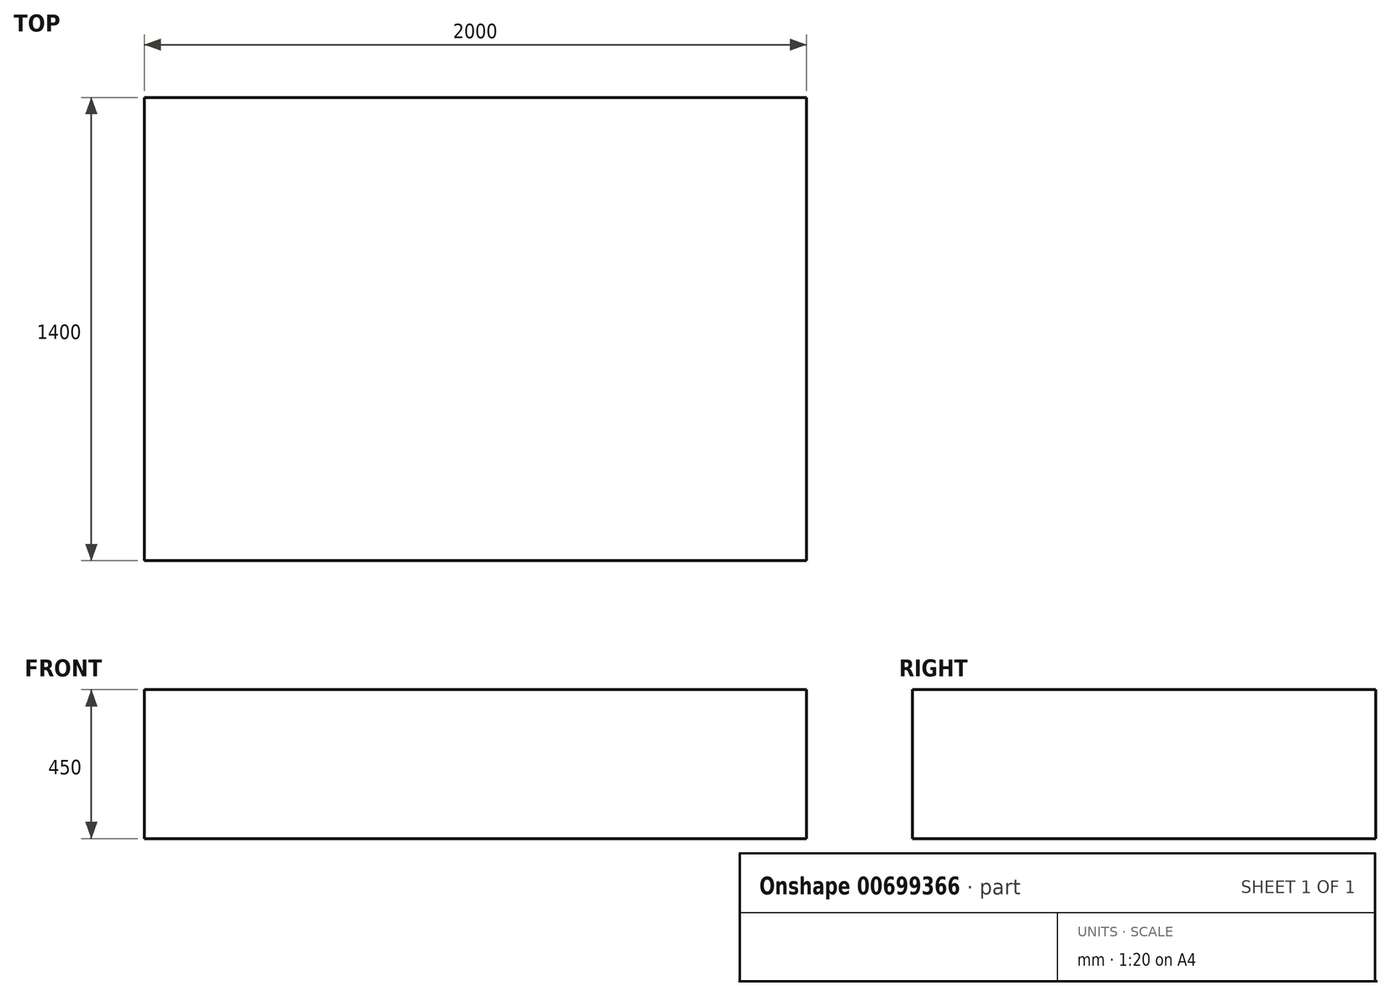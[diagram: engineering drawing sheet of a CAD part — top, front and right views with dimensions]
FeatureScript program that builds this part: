
annotation { "Feature Type Name" : "Feature", "Feature Type Description" : "" }
export const myFeature = defineFeature(function(context is Context, id is Id, definition is map)
    precondition{}
    {
        {
            var Q0;
            Q0=qCreatedBy(makeId("Top.planeOp"),FACE);
            var sketch = newSketch(context, id + "F0", { "sketchPlane" : qUnion([Q0])});
            skLineSegment(sketch, "E0.bottom", {"start": v(0, 0) * mm, "end": v(2000, 0) * mm});
            skLineSegment(sketch, "E0.top", {"start": v(0, 1400) * mm, "end": v(2000, 1400) * mm});
            skLineSegment(sketch, "E0.left", {"start": v(0, 0) * mm, "end": v(0, 1400) * mm});
            skLineSegment(sketch, "E0.right", {"start": v(2000, 0) * mm, "end": v(2000, 1400) * mm});
            skSolve(sketch);
        }
        {
            var Q0;
            Q0 = qSketchRegion(id + "F0", true);
            extrude(context, id + "F1", {"entities" : qUnion([Q0]), "flatOperationType" : FlatOperationType.REMOVE, "depth" : 450 * mm, "offsetDistance" : 25 * mm, "domain" : OperationDomain.MODEL});
        }
    });
